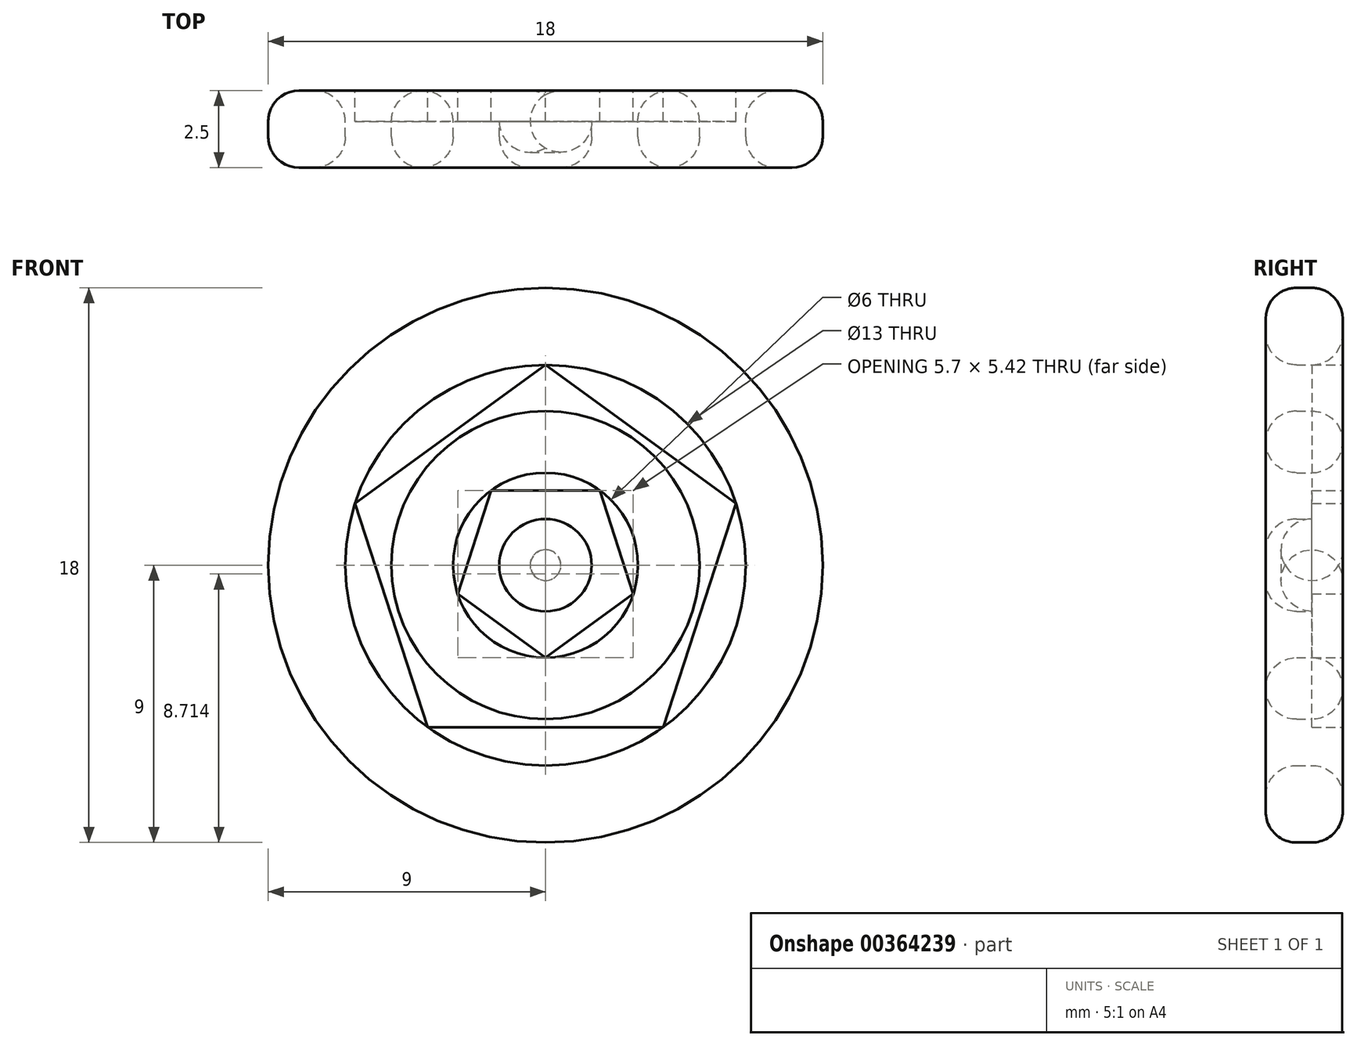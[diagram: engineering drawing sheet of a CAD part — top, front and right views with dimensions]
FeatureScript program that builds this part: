
annotation { "Feature Type Name" : "Feature", "Feature Type Description" : "" }
export const myFeature = defineFeature(function(context is Context, id is Id, definition is map)
    precondition{}
    {
        {
            var Q0;
            Q0=qCreatedBy(makeId("Front.planeOp"),FACE);
            var sketch = newSketch(context, id + "F0", { "sketchPlane" : qUnion([Q0])});
            skCircle(sketch, "E0", {"center": v(0, 0) * mm, "radius": 6.5 * mm});
            skCircle(sketch, "E1", {"center": v(0, 0) * mm, "radius": 9 * mm});
            skSolve(sketch);
        }
        {
            var Q0;
            Q0=makeQuery(id+"F0.imprint","IMPRINT",FACE,{"disambiguationData":[TD([[makeQuery(id+"F0.imprint","IMPRINT",EDGE,{"derivedFrom":sQuery(id+"F0.wireOp",EDGE,"E0")}),-1.0]])]});
            extrude(context, id + "F1", {"entities" : qUnion([Q0]), "depth" : 2.5 * mm});
        }
        {
            var Q0;
            Q0=makeQuery(id+"F1.opExtrude","CAP_EDGE",EDGE,{"disambiguationData":[OSD([sQuery(id+"F0.wireOp",EDGE,"E1")])],"isStart":false});
            var Q1;
            Q1=makeQuery(id+"F1.opExtrude","CAP_EDGE",EDGE,{"disambiguationData":[OSD([sQuery(id+"F0.wireOp",EDGE,"E1")])],"isStart":true});
            var Q2;
            Q2=makeQuery(id+"F1.opExtrude","CAP_EDGE",EDGE,{"disambiguationData":[OSD([sQuery(id+"F0.wireOp",EDGE,"E0")])],"isStart":true});
            var Q3;
            Q3=makeQuery(id+"F1.opExtrude","CAP_EDGE",EDGE,{"disambiguationData":[OSD([sQuery(id+"F0.wireOp",EDGE,"E0")])],"isStart":false});
            fillet(context, id + "F2", {"entities" : qUnion([Q0, Q1, Q2, Q3]), "radius" : 1 * mm, "tangentPropagation" : true, "allowEdgeOverflow" : false});
        }
        {
            var Q0;
            Q0=qCreatedBy(makeId("Front.planeOp"),FACE);
            var sketch = newSketch(context, id + "F3", { "sketchPlane" : qUnion([Q0])});
            skCircle(sketch, "E2", {"center": v(0, 0) * mm, "radius": 5 * mm});
            skCircle(sketch, "E3", {"center": v(0, 0) * mm, "radius": 3 * mm});
            skCircle(sketch, "E4", {"center": v(0, 0) * mm, "radius": 1.5 * mm});
            skLineSegment(sketch, "E5", {"start": v(0, 7.52) * mm, "end": v(0, 0) * mm});
            skLineSegment(sketch, "E6", {"start": v(0, -7.51) * mm, "end": v(0, 0) * mm});
            skLineSegment(sketch, "E7", {"start": v(7.51, 0) * mm, "end": v(0, 0) * mm});
            skLineSegment(sketch, "E8", {"start": v(-7.45, 0) * mm, "end": v(0, 0) * mm});
            skSolve(sketch);
        }
        {
            var Q0;
            {var subQ0=sQuery(id+"F3.wireOp",EDGE,"E5");var subQ1=sQuery(id+"F3.wireOp",EDGE,"E2");var subQ2=makeQuery(id+"F3.imprint","INTERSECT",VERTEX,{"derivedFrom":[subQ1,subQ0]});Q0=makeQuery(id+"F3.imprint","IMPRINT",FACE,{"disambiguationData":[TD([[makeQuery(id+"F3.imprint","IMPRINT",EDGE,{"disambiguationData":[TD([[subQ2,1.0]])],"derivedFrom":subQ1}),1.0]])]});}
            var Q1;
            {var subQ0=sQuery(id+"F3.wireOp",EDGE,"E5");var subQ1=sQuery(id+"F3.wireOp",EDGE,"E2");var subQ2=makeQuery(id+"F3.imprint","INTERSECT",VERTEX,{"derivedFrom":[subQ1,subQ0]});Q1=makeQuery(id+"F3.imprint","IMPRINT",FACE,{"disambiguationData":[TD([[makeQuery(id+"F3.imprint","IMPRINT",EDGE,{"disambiguationData":[TD([[subQ2,-1.0]])],"derivedFrom":subQ1}),1.0]])]});}
            var Q2;
            {var subQ0=sQuery(id+"F3.wireOp",EDGE,"E8");var subQ1=sQuery(id+"F3.wireOp",EDGE,"E2");var subQ2=makeQuery(id+"F3.imprint","INTERSECT",VERTEX,{"derivedFrom":[subQ1,subQ0]});Q2=makeQuery(id+"F3.imprint","IMPRINT",FACE,{"disambiguationData":[TD([[makeQuery(id+"F3.imprint","IMPRINT",EDGE,{"disambiguationData":[TD([[subQ2,-1.0]])],"derivedFrom":subQ1}),1.0]])]});}
            var Q3;
            {var subQ0=sQuery(id+"F3.wireOp",EDGE,"E7");var subQ1=sQuery(id+"F3.wireOp",EDGE,"E2");var subQ2=makeQuery(id+"F3.imprint","INTERSECT",VERTEX,{"derivedFrom":[subQ1,subQ0]});Q3=makeQuery(id+"F3.imprint","IMPRINT",FACE,{"disambiguationData":[TD([[makeQuery(id+"F3.imprint","IMPRINT",EDGE,{"disambiguationData":[TD([[subQ2,1.0]])],"derivedFrom":subQ1}),1.0]])]});}
            var Q4;
            {var subQ0=sQuery(id+"F3.wireOp",EDGE,"E7");var subQ1=sQuery(id+"F3.wireOp",EDGE,"E4");var subQ2=makeQuery(id+"F3.imprint","INTERSECT",VERTEX,{"derivedFrom":[subQ1,subQ0]});Q4=makeQuery(id+"F3.imprint","IMPRINT",FACE,{"disambiguationData":[TD([[makeQuery(id+"F3.imprint","IMPRINT",EDGE,{"disambiguationData":[TD([[subQ2,1.0]])],"derivedFrom":subQ1}),1.0]])]});}
            var Q5;
            {var subQ0=sQuery(id+"F3.wireOp",EDGE,"E5");var subQ1=sQuery(id+"F3.wireOp",EDGE,"E4");var subQ2=makeQuery(id+"F3.imprint","INTERSECT",VERTEX,{"derivedFrom":[subQ1,subQ0]});Q5=makeQuery(id+"F3.imprint","IMPRINT",FACE,{"disambiguationData":[TD([[makeQuery(id+"F3.imprint","IMPRINT",EDGE,{"disambiguationData":[TD([[subQ2,1.0]])],"derivedFrom":subQ1}),1.0]])]});}
            var Q6;
            {var subQ0=sQuery(id+"F3.wireOp",EDGE,"E5");var subQ1=sQuery(id+"F3.wireOp",EDGE,"E4");var subQ2=makeQuery(id+"F3.imprint","INTERSECT",VERTEX,{"derivedFrom":[subQ1,subQ0]});Q6=makeQuery(id+"F3.imprint","IMPRINT",FACE,{"disambiguationData":[TD([[makeQuery(id+"F3.imprint","IMPRINT",EDGE,{"disambiguationData":[TD([[subQ2,-1.0]])],"derivedFrom":subQ1}),1.0]])]});}
            var Q7;
            {var subQ0=sQuery(id+"F3.wireOp",EDGE,"E8");var subQ1=sQuery(id+"F3.wireOp",EDGE,"E4");var subQ2=makeQuery(id+"F3.imprint","INTERSECT",VERTEX,{"derivedFrom":[subQ1,subQ0]});Q7=makeQuery(id+"F3.imprint","IMPRINT",FACE,{"disambiguationData":[TD([[makeQuery(id+"F3.imprint","IMPRINT",EDGE,{"disambiguationData":[TD([[subQ2,-1.0]])],"derivedFrom":subQ1}),1.0]])]});}
            extrude(context, id + "F4", {"entities" : qUnion([Q0, Q1, Q2, Q3, Q4, Q5, Q6, Q7]), "depth" : 2.5 * mm});
        }
        {
            var Q0;
            Q0=makeQuery(id+"F4.opExtrude","CAP_EDGE",EDGE,{"disambiguationData":[OSD([sQuery(id+"F3.wireOp",EDGE,"E2")])],"isStart":true});
            var Q1;
            Q1=makeQuery(id+"F4.opExtrude","CAP_EDGE",EDGE,{"disambiguationData":[OSD([sQuery(id+"F3.wireOp",EDGE,"E2")])],"isStart":false});
            var Q2;
            Q2=makeQuery(id+"F4.opExtrude","CAP_EDGE",EDGE,{"disambiguationData":[OSD([sQuery(id+"F3.wireOp",EDGE,"E4")])],"isStart":false});
            var Q3;
            Q3=makeQuery(id+"F4.opExtrude","CAP_EDGE",EDGE,{"disambiguationData":[OSD([sQuery(id+"F3.wireOp",EDGE,"E4")])],"isStart":true});
            var Q4;
            Q4=makeQuery(id+"F4.opExtrude","CAP_EDGE",EDGE,{"disambiguationData":[OSD([sQuery(id+"F3.wireOp",EDGE,"E3")])],"isStart":true});
            var Q5;
            Q5=makeQuery(id+"F4.opExtrude","CAP_EDGE",EDGE,{"disambiguationData":[OSD([sQuery(id+"F3.wireOp",EDGE,"E3")])],"isStart":false});
            fillet(context, id + "F5", {"entities" : qUnion([Q0, Q1, Q2, Q3, Q4, Q5]), "radius" : 1 * mm, "tangentPropagation" : true, "allowEdgeOverflow" : false});
        }
        {
            var Q0;
            Q0=qCreatedBy(makeId("Front.planeOp"),FACE);
            var sketch = newSketch(context, id + "F6", { "sketchPlane" : qUnion([Q0])});
            skCircle(sketch, "E9.cCircle", {"center": v(0, 0) * mm, "radius": 3 * mm, "construction": true});
            skLineSegment(sketch, "E9.0", {"start": v(0, -3) * mm, "end": v(-2.85, -0.93) * mm});
            skLineSegment(sketch, "E9.1", {"start": v(-2.85, -0.93) * mm, "end": v(-1.76, 2.42) * mm});
            skLineSegment(sketch, "E9.2", {"start": v(-1.76, 2.42) * mm, "end": v(1.76, 2.42) * mm});
            skLineSegment(sketch, "E9.3", {"start": v(1.76, 2.42) * mm, "end": v(2.85, -0.93) * mm});
            skLineSegment(sketch, "E9.4", {"start": v(2.85, -0.93) * mm, "end": v(0, -3) * mm});
            skCircle(sketch, "E10.cCircle", {"center": v(0, 0) * mm, "radius": 6.5 * mm, "construction": true});
            skLineSegment(sketch, "E10.0", {"start": v(0, 6.5) * mm, "end": v(6.18, 2) * mm});
            skLineSegment(sketch, "E10.1", {"start": v(6.18, 2) * mm, "end": v(3.82, -5.26) * mm});
            skLineSegment(sketch, "E10.2", {"start": v(3.82, -5.26) * mm, "end": v(-3.82, -5.26) * mm});
            skLineSegment(sketch, "E10.3", {"start": v(-3.82, -5.26) * mm, "end": v(-6.18, 2) * mm});
            skLineSegment(sketch, "E10.4", {"start": v(-6.18, 2) * mm, "end": v(0, 6.5) * mm});
            skSolve(sketch);
        }
        {
            var Q0;
            Q0=makeQuery(id+"F6.imprint","IMPRINT",FACE,{"disambiguationData":[TD([[makeQuery(id+"F6.imprint","IMPRINT",EDGE,{"derivedFrom":sQuery(id+"F6.wireOp",EDGE,"E9.0")}),1.0]])]});
            extrude(context, id + "F7", {"entities" : qUnion([Q0]), "depth" : 1 * mm});
        }
    });
